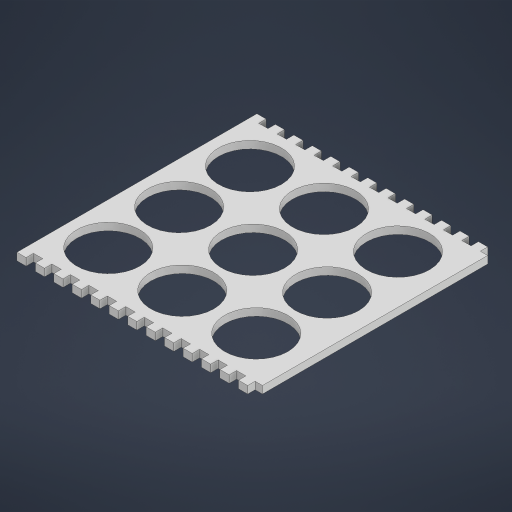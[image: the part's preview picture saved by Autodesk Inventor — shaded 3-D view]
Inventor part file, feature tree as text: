
AUTODESK INVENTOR PART (.ipt)
format: ipt  version: 2023 (Build 270158030, 158C)  size: 387,072 bytes
history: native  units: mm
features: extrude x2, sketch x2, mirror x1
ambient origin geometry x8: Origin, YZ Plane, XZ Plane, XY Plane, X Axis, Y Axis, Z Axis, Center Point
bodies: Solid1 (feature_tree)
feature tree (5):
  extrude  "Extrusion1"  Depth=4.0mm TaperAngle=0.0deg
  mirror  "Mirror1"
  extrude  "Extrusion2"  Depth=6.5mm TaperAngle=0.0deg
  sketch  "Sketch1"  dims[d0=180.0deg d1=4.0mm d2=0.0mm]
  sketch  "Sketch2"  dims[d3=132.004478mm d5=0.0mm d6=3.880396mm d7=47.003386mm d11=8.0mm d12=6.5mm d13=0.0mm]
